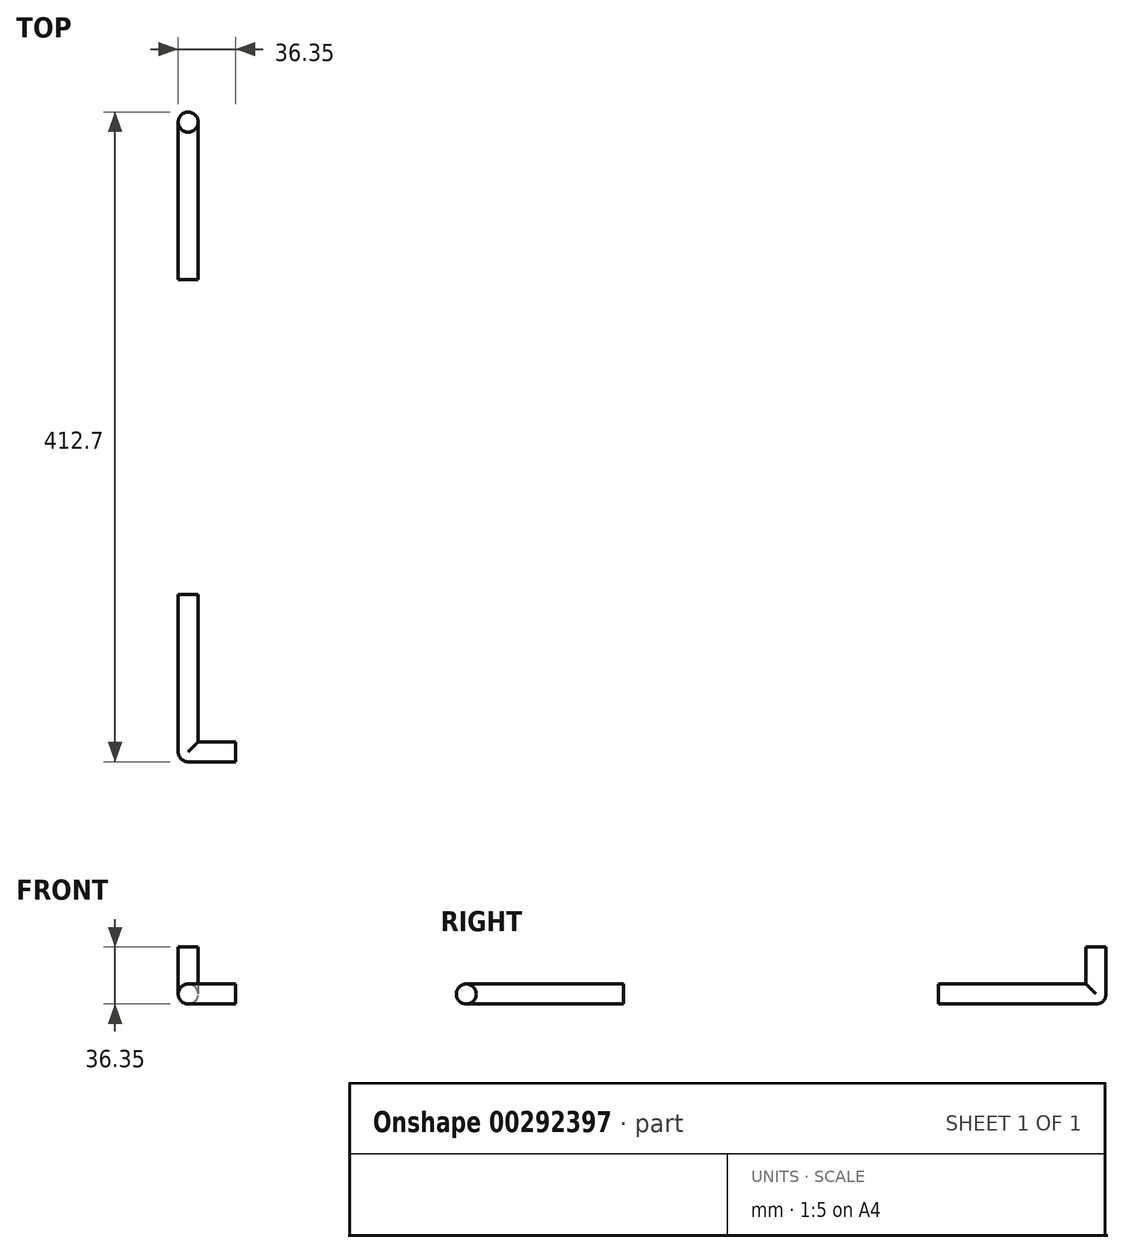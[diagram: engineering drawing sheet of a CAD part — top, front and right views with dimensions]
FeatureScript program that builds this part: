
annotation { "Feature Type Name" : "Feature", "Feature Type Description" : "" }
export const myFeature = defineFeature(function(context is Context, id is Id, definition is map)
    precondition{}
    {
        {
            var Q0;
            Q0=qCreatedBy(makeId("Top.planeOp"),FACE);
            var sketch = newSketch(context, id + "F0", { "sketchPlane" : qUnion([Q0])});
            skCircle(sketch, "E0", {"center": v(0, 0) * mm, "radius": 6.35 * mm});
            skSolve(sketch);
        }
        {
            var Q0;
            Q0 = qSketchRegion(id + "F0", true);
            extrude(context, id + "F1", {"entities" : qUnion([Q0]), "depth" : 30 * mm});
        }
        {
            var Q0;
            Q0=qCreatedBy(makeId("Front.planeOp"),FACE);
            var sketch = newSketch(context, id + "F2", { "sketchPlane" : qUnion([Q0])});
            skCircle(sketch, "E1", {"center": v(0, 0) * mm, "radius": 6.35 * mm});
            skSolve(sketch);
        }
        {
            var Q0;
            Q0 = qSketchRegion(id + "F2", true);
            extrude(context, id + "F3", {"entities" : qUnion([Q0]), "operationType" : NewBodyOperationType.ADD, "depth" : 100 * mm});
        }
        {
            var Q0;
            Q0=makeQuery(id+"F1.opExtrude","CAP_FACE",FACE,{"disambiguationData":[OSD([sQuery(id+"F0.wireOp",EDGE,"E0")])],"isStart":true});
            var Q1;
            Q1=makeQuery(id+"F3.boolean.opBoolean","INTERSECT",EDGE,{"derivedFrom":[makeQuery(id+"F1.opExtrude","CAP_FACE",FACE,{"disambiguationData":[OSD([sQuery(id+"F0.wireOp",EDGE,"E0")])],"isStart":true}),makeQuery(id+"F3.opExtrude","CAP_FACE",FACE,{"disambiguationData":[OSD([sQuery(id+"F2.wireOp",EDGE,"E1")])],"isStart":true})]});
            revolve(context, id + "F4", {"operationType" : NewBodyOperationType.ADD, "entities" : qUnion([Q0]), "axis" : qUnion([Q1]), "revolveType" : RevolveType.FULL});
        }
        {
            var Q0;
            Q0=qCreatedBy(makeId("Front.planeOp"),FACE);
            cPlane(context, id + "F5", {"entities" : qUnion([Q0]), "cplaneType" : CPlaneType.OFFSET, "offset" : 200 * mm, "width" : 150 * mm, "height" : 150 * mm});
        }
        {
            var Q0;
            Q0=makeQuery(id+"F1.opExtrude","SWEPT_BODY",BODY,{"disambiguationData":[OSD([sQuery(id+"F0.wireOp",EDGE,"E0")])]});
            var Q1;
            Q1=qCreatedBy(id+"F5.planeOp",FACE);
            mirror(context, id + "F6", {"entities" : qUnion([Q0]), "mirrorPlane" : qUnion([Q1])});
        }
        {
            var Q0;
            Q0=makeQuery(id+"F6.opPattern","COPY",BODY,{"derivedFrom":makeQuery(id+"F1.opExtrude","SWEPT_BODY",BODY,{"disambiguationData":[OSD([sQuery(id+"F0.wireOp",EDGE,"E0")])]}),"instanceName":"1"});
            var Q1;
            Q1=makeQuery(id+"F6.opPattern","COPY",FACE,{"derivedFrom":makeQuery(id+"F3.opExtrude","SWEPT_FACE",FACE,{"disambiguationData":[OSD([sQuery(id+"F2.wireOp",EDGE,"E1")])]}),"instanceName":"1"});
            transform(context, id + "F7", {"entities" : qUnion([Q0]), "transformType" : TransformType.ROTATION, "transformAxis" : qUnion([Q1]), "angle" : 90 * degree, "oppositeDirection" : true, "makeCopy" : false});
        }
    });
